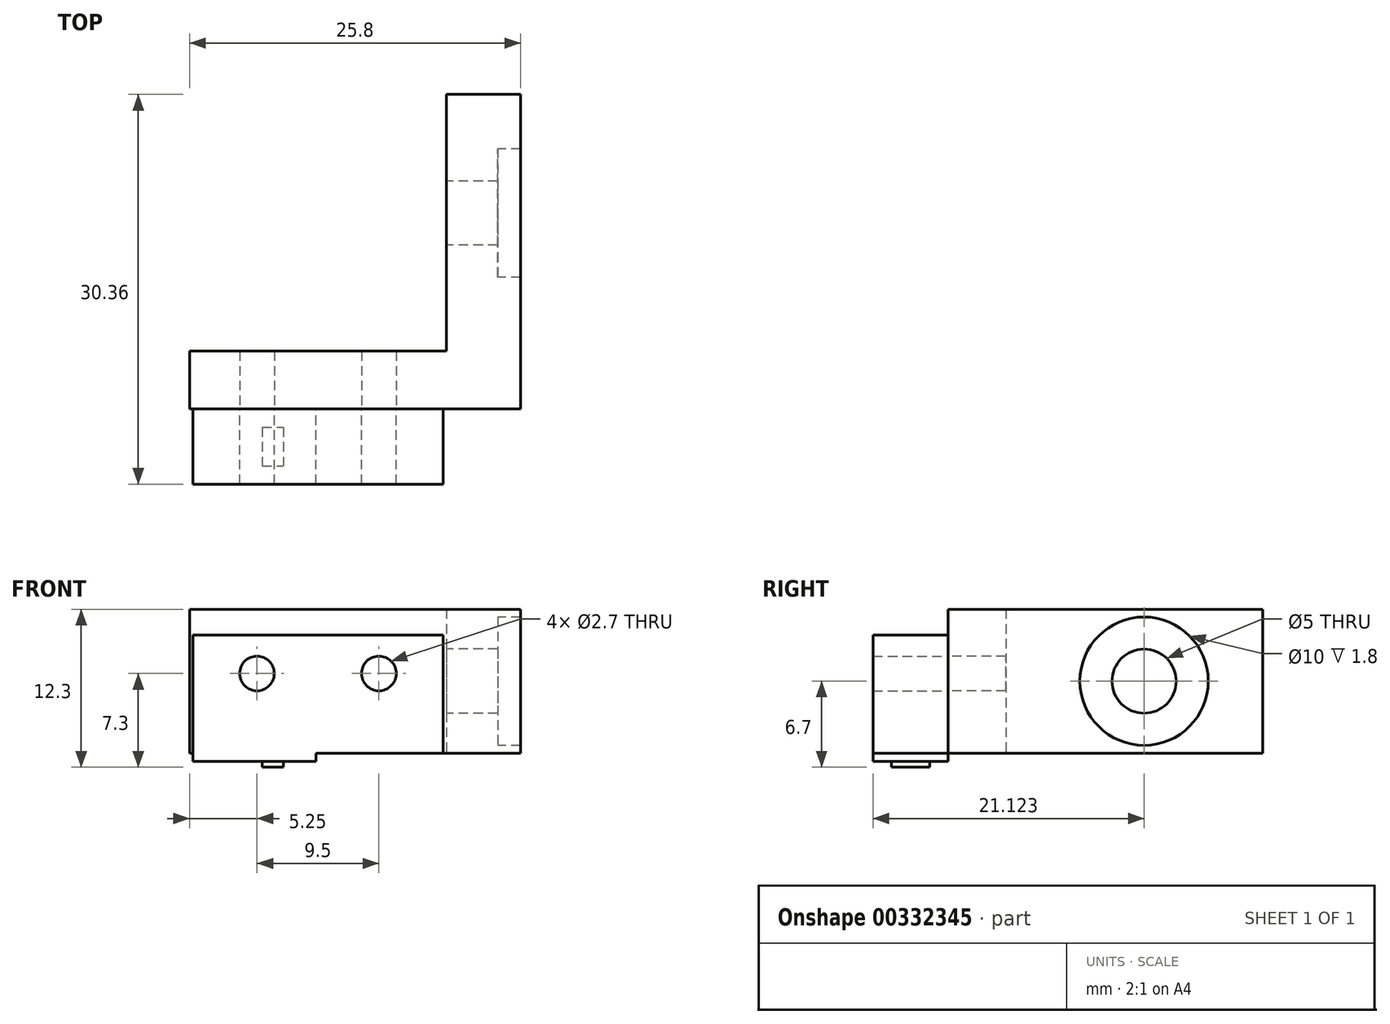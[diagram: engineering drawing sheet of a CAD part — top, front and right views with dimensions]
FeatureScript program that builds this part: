
annotation { "Feature Type Name" : "Feature", "Feature Type Description" : "" }
export const myFeature = defineFeature(function(context is Context, id is Id, definition is map)
    precondition{}
    {
        {
            var Q0;
            Q0=qCreatedBy(makeId("Front.planeOp"),FACE);
            var sketch = newSketch(context, id + "F0", { "sketchPlane" : qUnion([Q0])});
            skLineSegment(sketch, "E0.bottom", {"start": v(9.75, -4.6) * mm, "end": v(-0.15, -4.6) * mm});
            skLineSegment(sketch, "E0.top", {"start": v(9.75, 4.6) * mm, "end": v(-9.75, 4.6) * mm});
            skLineSegment(sketch, "E0.left", {"start": v(9.75, -4.6) * mm, "end": v(9.75, 4.6) * mm});
            skLineSegment(sketch, "E0.right", {"start": v(-9.75, -4.6) * mm, "end": v(-9.75, 4.6) * mm});
            skPoint(sketch, "E0.middle", {"position": v(0, 0) * mm});
            skLineSegment(sketch, "E1", {"start": v(-0.15, -4.6) * mm, "end": v(-9.75, -4.6) * mm});
            skLineSegment(sketch, "E2.0", {"start": v(-0.15, -5.25) * mm, "end": v(-9.75, -5.25) * mm});
            skLineSegment(sketch, "E3", {"start": v(-9.75, -4.6) * mm, "end": v(-9.75, -5.25) * mm});
            skLineSegment(sketch, "E4", {"start": v(-0.15, -4.6) * mm, "end": v(-0.15, -5.25) * mm});
            skCircle(sketch, "E5", {"center": v(-4.75, 1.6) * mm, "radius": 1.35 * mm});
            skCircle(sketch, "E6", {"center": v(4.75, 1.6) * mm, "radius": 1.35 * mm});
            skSolve(sketch);
        }
        {
            var Q0;
            Q0=makeQuery(id+"F0.imprint","IMPRINT",FACE,{"disambiguationData":[TD([[makeQuery(id+"F0.imprint","IMPRINT",EDGE,{"derivedFrom":sQuery(id+"F0.wireOp",EDGE,"E0.bottom")}),-1.0]])]});
            var Q1;
            Q1=makeQuery(id+"F0.imprint","IMPRINT",FACE,{"disambiguationData":[TD([[makeQuery(id+"F0.imprint","IMPRINT",EDGE,{"derivedFrom":sQuery(id+"F0.wireOp",EDGE,"E1")}),1.0]])]});
            extrude(context, id + "F1", {"entities" : qUnion([Q0, Q1]), "depth" : 2.93 * mm, "hasSecondDirection" : true, "secondDirectionOppositeDirection" : true, "secondDirectionDepth" : 2.93 * mm});
        }
        {
            var Q0;
            Q0=qCreatedBy(makeId("Top.planeOp"),FACE);
            var sketch = newSketch(context, id + "F2", { "sketchPlane" : qUnion([Q0])});
            skLineSegment(sketch, "E7.bottom", {"start": v(-2.7, -1.5) * mm, "end": v(-4.35, -1.5) * mm});
            skLineSegment(sketch, "E7.top", {"start": v(-2.7, 1.5) * mm, "end": v(-4.35, 1.5) * mm});
            skLineSegment(sketch, "E7.left", {"start": v(-2.7, -1.5) * mm, "end": v(-2.7, 1.5) * mm});
            skLineSegment(sketch, "E7.right", {"start": v(-4.35, -1.5) * mm, "end": v(-4.35, 1.5) * mm});
            skPoint(sketch, "E7.middle", {"position": v(-3.52, 0) * mm});
            skSolve(sketch);
        }
        {
            var Q0;
            Q0=makeQuery(id+"F2.imprint","IMPRINT",FACE,{"disambiguationData":[TD([[makeQuery(id+"F2.imprint","IMPRINT",EDGE,{"derivedFrom":sQuery(id+"F2.wireOp",EDGE,"E7.bottom")}),-1.0]])]});
            extrude(context, id + "F3", {"entities" : qUnion([Q0]), "operationType" : NewBodyOperationType.ADD, "oppositeDirection" : true, "depth" : 5.7 * mm});
        }
        {
            var Q0;
            Q0=qCreatedBy(makeId("Top.planeOp"),FACE);
            var sketch = newSketch(context, id + "F4", { "sketchPlane" : qUnion([Q0])});
            skLineSegment(sketch, "E8.bottom", {"start": v(10, 2.93) * mm, "end": v(-10, 2.93) * mm});
            skLineSegment(sketch, "E8.top", {"start": v(10, 7.43) * mm, "end": v(-10, 7.43) * mm});
            skLineSegment(sketch, "E8.left", {"start": v(10, 2.93) * mm, "end": v(10, 7.43) * mm});
            skLineSegment(sketch, "E8.right", {"start": v(-10, 2.93) * mm, "end": v(-10, 7.43) * mm});
            skPoint(sketch, "E8.middle", {"position": v(0, 5.18) * mm});
            skLineSegment(sketch, "E9.bottom", {"start": v(2.95, 7.43) * mm, "end": v(-2.95, 7.43) * mm});
            skLineSegment(sketch, "E9.top", {"start": v(2.95, 9.93) * mm, "end": v(-2.95, 9.93) * mm});
            skLineSegment(sketch, "E9.left", {"start": v(2.95, 7.43) * mm, "end": v(2.95, 9.93) * mm});
            skLineSegment(sketch, "E9.right", {"start": v(-2.95, 7.43) * mm, "end": v(-2.95, 9.93) * mm});
            skPoint(sketch, "E9.middle", {"position": v(0, 8.68) * mm});
            skLineSegment(sketch, "E10.bottom", {"start": v(10, 2.93) * mm, "end": v(15.8, 2.93) * mm});
            skLineSegment(sketch, "E10.top", {"start": v(10, 27.43) * mm, "end": v(15.8, 27.43) * mm});
            skLineSegment(sketch, "E10.left", {"start": v(10, 2.93) * mm, "end": v(10, 27.43) * mm});
            skLineSegment(sketch, "E10.right", {"start": v(15.8, 2.93) * mm, "end": v(15.8, 27.43) * mm});
            skLineSegment(sketch, "E11.bottom", {"start": v(15.8, 2.93) * mm, "end": v(11.3, 2.93) * mm});
            skLineSegment(sketch, "E12", {"start": v(10, -2.93) * mm, "end": v(15.8, 2.93) * mm});
            skLineSegment(sketch, "E13", {"start": v(10, -2.93) * mm, "end": v(9.75, -2.93) * mm});
            skLineSegment(sketch, "E14", {"start": v(9.75, -2.93) * mm, "end": v(9.75, 2.93) * mm});
            skLineSegment(sketch, "E15", {"start": v(9.75, 2.93) * mm, "end": v(10, 2.93) * mm});
            skSolve(sketch);
        }
        {
            var Q0;
            {var subQ5=sQuery(id+"F4.wireOp",EDGE,"E8.bottom");Q0=makeQuery(id+"F4.imprint","IMPRINT",FACE,{"disambiguationData":[TD([[makeQuery(id+"F4.imprint","IMPRINT",EDGE,{"derivedFrom":subQ5}),-1.0]])]});}
            var Q1;
            Q1=makeQuery(id+"F4.imprint","IMPRINT",FACE,{"disambiguationData":[TD([[makeQuery(id+"F4.imprint","IMPRINT",EDGE,{"derivedFrom":sQuery(id+"F4.wireOp",EDGE,"E11.bottom")}),1.0]])]});
            var Q2;
            {var subQ2=sQuery(id+"F4.wireOp",EDGE,"E10.top");Q2=makeQuery(id+"F4.imprint","IMPRINT",FACE,{"disambiguationData":[TD([[makeQuery(id+"F4.imprint","IMPRINT",EDGE,{"derivedFrom":subQ2}),-1.0]])]});}
            var Q3;
            Q3=makeQuery(id+"F4.imprint","IMPRINT",FACE,{"disambiguationData":[TD([[makeQuery(id+"F4.imprint","IMPRINT",EDGE,{"derivedFrom":sQuery(id+"F4.wireOp",EDGE,"E9.bottom")}),-1.0]])]});
            extrude(context, id + "F5", {"entities" : qUnion([Q0, Q1, Q2, Q3]), "depth" : 6.6 * mm, "hasSecondDirection" : true, "secondDirectionOppositeDirection" : true, "secondDirectionDepth" : 4.6 * mm});
        }
        {
            var Q0;
            Q0=makeQuery(id+"F0.imprint","IMPRINT",FACE,{"disambiguationData":[TD([[makeQuery(id+"F0.imprint","IMPRINT",EDGE,{"derivedFrom":sQuery(id+"F0.wireOp",EDGE,"E5")}),1.0]])]});
            var Q1;
            Q1=makeQuery(id+"F0.imprint","IMPRINT",FACE,{"disambiguationData":[TD([[makeQuery(id+"F0.imprint","IMPRINT",EDGE,{"derivedFrom":sQuery(id+"F0.wireOp",EDGE,"E6")}),1.0]])]});
            extrude(context, id + "F6", {"entities" : qUnion([Q0, Q1]), "operationType" : NewBodyOperationType.REMOVE, "oppositeDirection" : true, "depth" : 25 * mm});
        }
        {
            var Q0;
            Q0=makeQuery(id+"F5.opExtrude","SWEPT_FACE",FACE,{"disambiguationData":[OSD([sQuery(id+"F4.wireOp",EDGE,"E10.left")])]});
            cPlane(context, id + "F7", {"entities" : qUnion([Q0]), "cplaneType" : CPlaneType.OFFSET, "offset" : 0 * mm, "width" : 150 * mm, "height" : 150 * mm});
        }
        {
            var Q0;
            Q0=qCreatedBy(id+"F7.planeOp",FACE);
            var sketch = newSketch(context, id + "F8", { "sketchPlane" : qUnion([Q0])});
            skCircle(sketch, "E16", {"center": v(-18.2, 1) * mm, "radius": 2.5 * mm});
            skCircle(sketch, "E17", {"center": v(-18.2, 1) * mm, "radius": 5 * mm});
            skSolve(sketch);
        }
        {
            var Q0;
            Q0=makeQuery(id+"F8.imprint","IMPRINT",FACE,{"disambiguationData":[TD([[makeQuery(id+"F8.imprint","IMPRINT",EDGE,{"derivedFrom":sQuery(id+"F8.wireOp",EDGE,"E16")}),1.0]])]});
            extrude(context, id + "F9", {"entities" : qUnion([Q0]), "operationType" : NewBodyOperationType.REMOVE, "oppositeDirection" : true, "depth" : 25 * mm});
        }
        {
            var Q0;
            Q0=makeQuery(id+"F8.imprint","IMPRINT",FACE,{"disambiguationData":[TD([[makeQuery(id+"F8.imprint","IMPRINT",EDGE,{"derivedFrom":sQuery(id+"F8.wireOp",EDGE,"E16")}),-1.0]])]});
            extrude(context, id + "F10", {"entities" : qUnion([Q0]), "operationType" : NewBodyOperationType.REMOVE, "oppositeDirection" : true, "depth" : 25 * mm, "hasSecondDirection" : true, "secondDirectionOppositeDirection" : true, "secondDirectionDepth" : 4 * mm});
        }
    });
